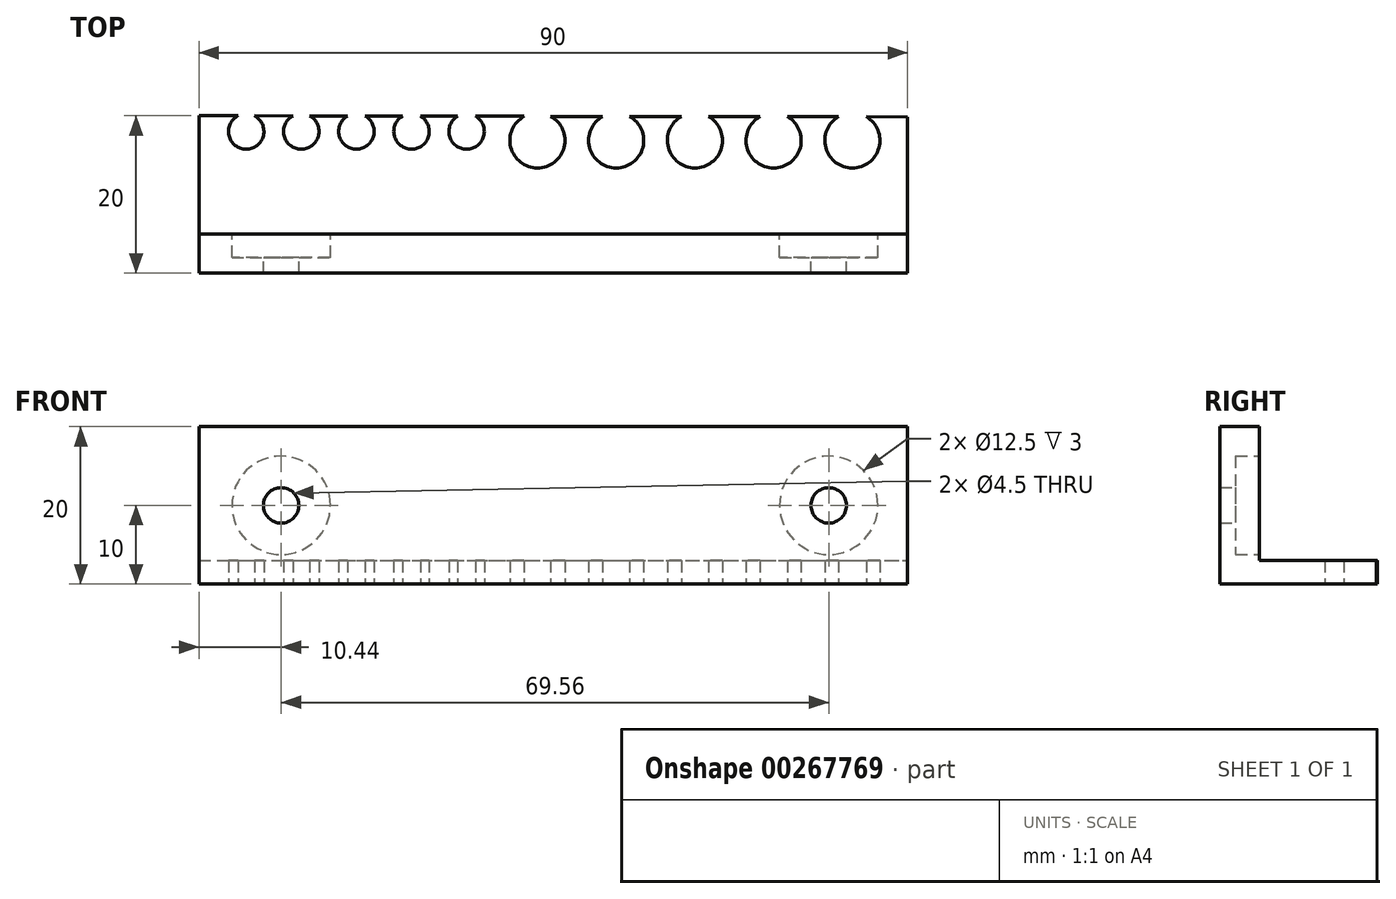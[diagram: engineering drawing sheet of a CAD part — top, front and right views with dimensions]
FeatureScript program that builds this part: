
annotation { "Feature Type Name" : "Feature", "Feature Type Description" : "" }
export const myFeature = defineFeature(function(context is Context, id is Id, definition is map)
    precondition{}
    {
        {
            var Q0;
            Q0=qCreatedBy(makeId("Top.planeOp"),FACE);
            var sketch = newSketch(context, id + "F0", { "sketchPlane" : qUnion([Q0])});
            skLineSegment(sketch, "E0.left", {"start": v(0, -5) * mm, "end": v(0, 15) * mm});
            skLineSegment(sketch, "E0.right", {"start": v(90, -5) * mm, "end": v(90, 14.86) * mm});
            skLineSegment(sketch, "E1.trimOffspring", {"start": v(0, 15) * mm, "end": v(4.95, 15) * mm});
            skLineSegment(sketch, "E2", {"start": v(0, -5) * mm, "end": v(90, -5) * mm});
            skPoint(sketch, "E3.orphan", {"position": v(0, 0) * mm});
            skLineSegment(sketch, "E4", {"start": v(0, 0) * mm, "end": v(90, 0) * mm});
            skLineSegment(sketch, "E5", {"start": v(90, 14.86) * mm, "end": v(90, 11.86) * mm});
            skArc(sketch, "E6", {"start": v(81.22, 14.87) * mm, "mid": v(83, 8.36) * mm, "end": v(84.8, 14.87) * mm});
            skArc(sketch, "E7", {"start": v(71.24, 14.88) * mm, "mid": v(73, 8.36) * mm, "end": v(74.77, 14.88) * mm});
            skArc(sketch, "E8", {"start": v(61.27, 14.9) * mm, "mid": v(63, 8.36) * mm, "end": v(64.74, 14.9) * mm});
            skArc(sketch, "E9", {"start": v(51.3, 14.91) * mm, "mid": v(53, 8.36) * mm, "end": v(54.72, 14.9) * mm});
            skArc(sketch, "E10", {"start": v(41.32, 14.93) * mm, "mid": v(43, 8.36) * mm, "end": v(44.7, 14.92) * mm});
            skLineSegment(sketch, "E11", {"start": v(0, 15) * mm, "end": v(0, 13) * mm});
            skArc(sketch, "E12", {"start": v(4.95, 15) * mm, "mid": v(6, 10.75) * mm, "end": v(7.05, 14.99) * mm});
            skArc(sketch, "E13", {"start": v(11.93, 14.98) * mm, "mid": v(13, 10.75) * mm, "end": v(14.08, 14.98) * mm});
            skArc(sketch, "E14", {"start": v(18.9, 14.97) * mm, "mid": v(20, 10.75) * mm, "end": v(21.1, 14.96) * mm});
            skArc(sketch, "E15", {"start": v(25.88, 14.95) * mm, "mid": v(27, 10.75) * mm, "end": v(28.12, 14.95) * mm});
            skArc(sketch, "E16", {"start": v(32.86, 14.94) * mm, "mid": v(34, 10.75) * mm, "end": v(35.14, 14.94) * mm});
            skLineSegment(sketch, "E17.trimOffspring", {"start": v(7.05, 14.99) * mm, "end": v(11.93, 14.98) * mm});
            skLineSegment(sketch, "E18.trimOffspring", {"start": v(14.08, 14.98) * mm, "end": v(18.9, 14.97) * mm});
            skLineSegment(sketch, "E19.trimOffspring", {"start": v(21.1, 14.96) * mm, "end": v(25.88, 14.95) * mm});
            skLineSegment(sketch, "E20.trimOffspring", {"start": v(28.12, 14.95) * mm, "end": v(32.86, 14.94) * mm});
            skLineSegment(sketch, "E21.trimOffspring", {"start": v(35.14, 14.94) * mm, "end": v(41.32, 14.93) * mm});
            skLineSegment(sketch, "E22.trimOffspring", {"start": v(44.7, 14.92) * mm, "end": v(51.3, 14.91) * mm});
            skLineSegment(sketch, "E23.trimOffspring", {"start": v(54.72, 14.9) * mm, "end": v(61.27, 14.9) * mm});
            skLineSegment(sketch, "E24.trimOffspring", {"start": v(64.74, 14.9) * mm, "end": v(71.24, 14.88) * mm});
            skLineSegment(sketch, "E25.trimOffspring", {"start": v(74.77, 14.88) * mm, "end": v(81.22, 14.87) * mm});
            skLineSegment(sketch, "E26.trimOffspring", {"start": v(84.8, 14.87) * mm, "end": v(90, 14.86) * mm});
            skSolve(sketch);
        }
        {
            var Q0;
            {var subQ0=sQuery(id+"F0.wireOp",EDGE,"E2");Q0=makeQuery(id+"F0.imprint","IMPRINT",FACE,{"disambiguationData":[TD([[makeQuery(id+"F0.imprint","IMPRINT",EDGE,{"derivedFrom":subQ0}),1.0]])]});}
            extrude(context, id + "F1", {"entities" : qUnion([Q0]), "depth" : 20 * mm});
        }
        {
            var Q0;
            Q0=makeQuery(id+"F1.opExtrude","SWEPT_FACE",FACE,{"disambiguationData":[OSD([sQuery(id+"F0.wireOp",EDGE,"E4")])]});
            var sketch = newSketch(context, id + "F2", { "sketchPlane" : qUnion([Q0])});
            skCircle(sketch, "E27", {"center": v(-10.44, 10) * mm, "radius": 6.25 * mm});
            skPoint(sketch, "E27.centerSnap0", {"position": v(0, 10) * mm});
            skCircle(sketch, "E28", {"center": v(-80, 10) * mm, "radius": 6.25 * mm});
            skPoint(sketch, "E28.centerSnap0", {"position": v(-90, 10) * mm});
            skCircle(sketch, "E29", {"center": v(-80, 10) * mm, "radius": 2.25 * mm});
            skCircle(sketch, "E30", {"center": v(-10.44, 10) * mm, "radius": 2.25 * mm});
            skSolve(sketch);
        }
        {
            var Q0;
            Q0 = qSketchRegion(id + "F2", true);
            extrude(context, id + "F3", {"entities" : qUnion([Q0]), "operationType" : NewBodyOperationType.REMOVE, "oppositeDirection" : true, "depth" : 3 * mm});
        }
        {
            var Q0;
            Q0=makeQuery(id+"F3.boolean.opBoolean","SPLIT",FACE,{"disambiguationData":[TD([makeQuery(id+"F3.opExtrude","SWEPT_FACE",FACE,{"disambiguationData":[OSD([sQuery(id+"F2.wireOp",EDGE,"E29")])]})])],"derivedFrom":makeQuery(id+"F1.opExtrude","SWEPT_FACE",FACE,{"disambiguationData":[OSD([sQuery(id+"F0.wireOp",EDGE,"E4")])]})});
            var Q1;
            Q1=makeQuery(id+"F3.boolean.opBoolean","SPLIT",FACE,{"disambiguationData":[TD([makeQuery(id+"F3.opExtrude","SWEPT_FACE",FACE,{"disambiguationData":[OSD([sQuery(id+"F2.wireOp",EDGE,"E30")])]})])],"derivedFrom":makeQuery(id+"F1.opExtrude","SWEPT_FACE",FACE,{"disambiguationData":[OSD([sQuery(id+"F0.wireOp",EDGE,"E4")])]})});
            extrude(context, id + "F4", {"entities" : qUnion([Q0, Q1]), "operationType" : NewBodyOperationType.REMOVE, "oppositeDirection" : true, "depth" : 25 * mm});
        }
        {
            var Q0;
            Q0=makeQuery(id+"F0.imprint","IMPRINT",FACE,{"disambiguationData":[TD([[makeQuery(id+"F0.imprint","IMPRINT",EDGE,{"derivedFrom":sQuery(id+"F0.wireOp",EDGE,"E1.trimOffspring")}),-1.0]])]});
            extrude(context, id + "F5", {"entities" : qUnion([Q0]), "operationType" : NewBodyOperationType.ADD, "depth" : 3 * mm});
        }
    });
